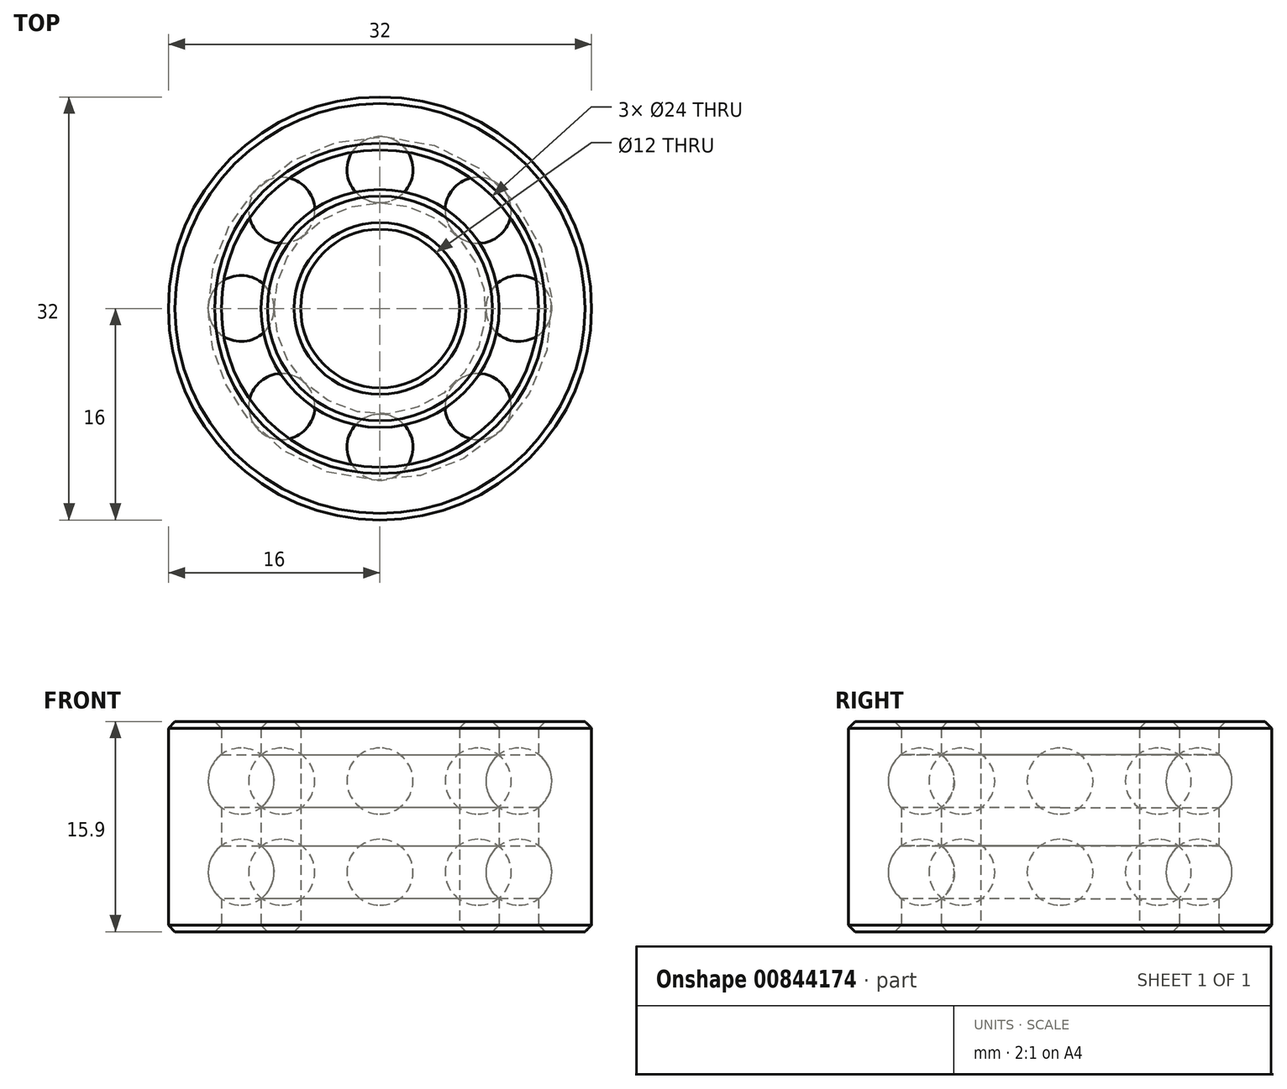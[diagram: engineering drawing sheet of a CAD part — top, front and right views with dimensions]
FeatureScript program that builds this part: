
annotation { "Feature Type Name" : "Feature", "Feature Type Description" : "" }
export const myFeature = defineFeature(function(context is Context, id is Id, definition is map)
    precondition{}
    {
        {
            var Q0;
            Q0=qCreatedBy(makeId("Top.planeOp"),FACE);
            var sketch = newSketch(context, id + "F0", { "sketchPlane" : qUnion([Q0])});
            skCircle(sketch, "E0", {"center": v(0, 0) * mm, "radius": 6 * mm});
            skCircle(sketch, "E1", {"center": v(0, 0) * mm, "radius": 16 * mm});
            skCircle(sketch, "E2", {"center": v(0, 0) * mm, "radius": 9 * mm});
            skCircle(sketch, "E3", {"center": v(0, 0) * mm, "radius": 12 * mm});
            skSolve(sketch);
        }
        {
            var Q0;
            Q0=makeQuery(id+"F0.imprint","IMPRINT",FACE,{"disambiguationData":[TD([[makeQuery(id+"F0.imprint","IMPRINT",EDGE,{"derivedFrom":sQuery(id+"F0.wireOp",EDGE,"E0")}),-1.0]])]});
            var Q1;
            Q1=makeQuery(id+"F0.imprint","IMPRINT",FACE,{"disambiguationData":[TD([[makeQuery(id+"F0.imprint","IMPRINT",EDGE,{"derivedFrom":sQuery(id+"F0.wireOp",EDGE,"E1")}),1.0]])]});
            extrude(context, id + "F1", {"entities" : qUnion([Q0, Q1]), "depth" : 15.9 * mm, "offsetDistance" : 25 * mm});
        }
        {
            var Q0;
            Q0=makeQuery(id+"F1.opExtrude","CAP_FACE",FACE,{"disambiguationData":[OSD([sQuery(id+"F0.wireOp",EDGE,"E1"),sQuery(id+"F0.wireOp",EDGE,"E3")])],"isStart":false});
            var Q1;
            Q1=makeQuery(id+"F1.opExtrude","CAP_FACE",FACE,{"disambiguationData":[OSD([sQuery(id+"F0.wireOp",EDGE,"E0"),sQuery(id+"F0.wireOp",EDGE,"E2")])],"isStart":false});
            var Q2;
            Q2=makeQuery(id+"F1.opExtrude","CAP_FACE",FACE,{"disambiguationData":[OSD([sQuery(id+"F0.wireOp",EDGE,"E1"),sQuery(id+"F0.wireOp",EDGE,"E3")])],"isStart":true});
            var Q3;
            Q3=makeQuery(id+"F1.opExtrude","CAP_FACE",FACE,{"disambiguationData":[OSD([sQuery(id+"F0.wireOp",EDGE,"E0"),sQuery(id+"F0.wireOp",EDGE,"E2")])],"isStart":true});
            chamfer(context, id + "F2", {"entities" : qUnion([Q0, Q1, Q2, Q3]), "width" : .5 * mm, "tangentPropagation" : true});
        }
        {
            var Q0;
            Q0=qCreatedBy(makeId("Front.planeOp"),FACE);
            var sketch = newSketch(context, id + "F3", { "sketchPlane" : qUnion([Q0])});
            skCircle(sketch, "E4", {"center": v(10.5, 11.4) * mm, "radius": 2.5 * mm});
            skCircle(sketch, "E5", {"center": v(10.5, 4.5) * mm, "radius": 2.5 * mm});
            skLineSegment(sketch, "E6", {"start": v(0, 17.94) * mm, "end": v(0, -2.67) * mm});
            skSolve(sketch);
        }
        {
            var Q0;
            Q0=qSketchRegion(id+"F3",true);
            var Q1;
            Q1=sQuery(id+"F3.wireOp",EDGE,"E6");
            revolve(context, id + "F4", {"operationType" : NewBodyOperationType.REMOVE, "surfaceOperationType" : NewSurfaceOperationType.NEW, "entities" : qUnion([Q0]), "axis" : qUnion([Q1]), "revolveType" : RevolveType.FULL, "oppositeDirection" : true});
        }
        {
            var Q0;
            Q0=qCreatedBy(makeId("Front.planeOp"),FACE);
            var sketch = newSketch(context, id + "F5", { "sketchPlane" : qUnion([Q0])});
            skArc(sketch, "E7", {"start": v(10.5, 8.9) * mm, "mid": v(13, 11.4) * mm, "end": v(10.5, 13.9) * mm});
            skArc(sketch, "E8", {"start": v(10.5, 2) * mm, "mid": v(13, 4.5) * mm, "end": v(10.5, 7) * mm});
            skLineSegment(sketch, "E9", {"start": v(10.5, 11.4) * mm, "end": v(10.5, 13.9) * mm});
            skLineSegment(sketch, "E10", {"start": v(10.5, 11.4) * mm, "end": v(10.5, 8.9) * mm});
            skLineSegment(sketch, "E11", {"start": v(10.5, 4.5) * mm, "end": v(10.5, 7) * mm});
            skLineSegment(sketch, "E12", {"start": v(10.5, 4.5) * mm, "end": v(10.5, 2) * mm});
            skSolve(sketch);
        }
        {
            var Q0;
            Q0=qSketchRegion(id+"F5",true);
            var Q1;
            Q1=sQuery(id+"F5.wireOp",EDGE,"E9");
            revolve(context, id + "F6", {"surfaceOperationType" : NewSurfaceOperationType.NEW, "entities" : qUnion([Q0]), "axis" : qUnion([Q1]), "revolveType" : RevolveType.FULL});
        }
        {
            var Q0;
            Q0=qCreatedBy(makeId("Front.planeOp"),FACE);
            var sketch = newSketch(context, id + "F7", { "sketchPlane" : qUnion([Q0])});
            skLineSegment(sketch, "E13", {"start": v(0, 47.8) * mm, "end": v(0, -43.73) * mm, "construction": true});
            skSolve(sketch);
        }
        {
            var Q0;
            Q0=makeQuery(id+"F6.opRevolve","SWEPT_BODY",BODY,{"disambiguationData":[OSD([sQuery(id+"F5.wireOp",EDGE,"E7"),sQuery(id+"F5.wireOp",EDGE,"E9"),sQuery(id+"F5.wireOp",EDGE,"E10")])]});
            var Q1;
            Q1=makeQuery(id+"F6.opRevolve","SWEPT_BODY",BODY,{"disambiguationData":[OSD([sQuery(id+"F5.wireOp",EDGE,"E8"),sQuery(id+"F5.wireOp",EDGE,"E11"),sQuery(id+"F5.wireOp",EDGE,"E12")])]});
            var Q2;
            Q2=sQuery(id+"F7.wireOp",EDGE,"E13");
            circularPattern(context, id + "F8", {"entities" : qUnion([Q0, Q1]), "axis" : qUnion([Q2]), "angle" : 360 * degree, "instanceCount" : 8, "equalSpace" : true});
        }
    });
